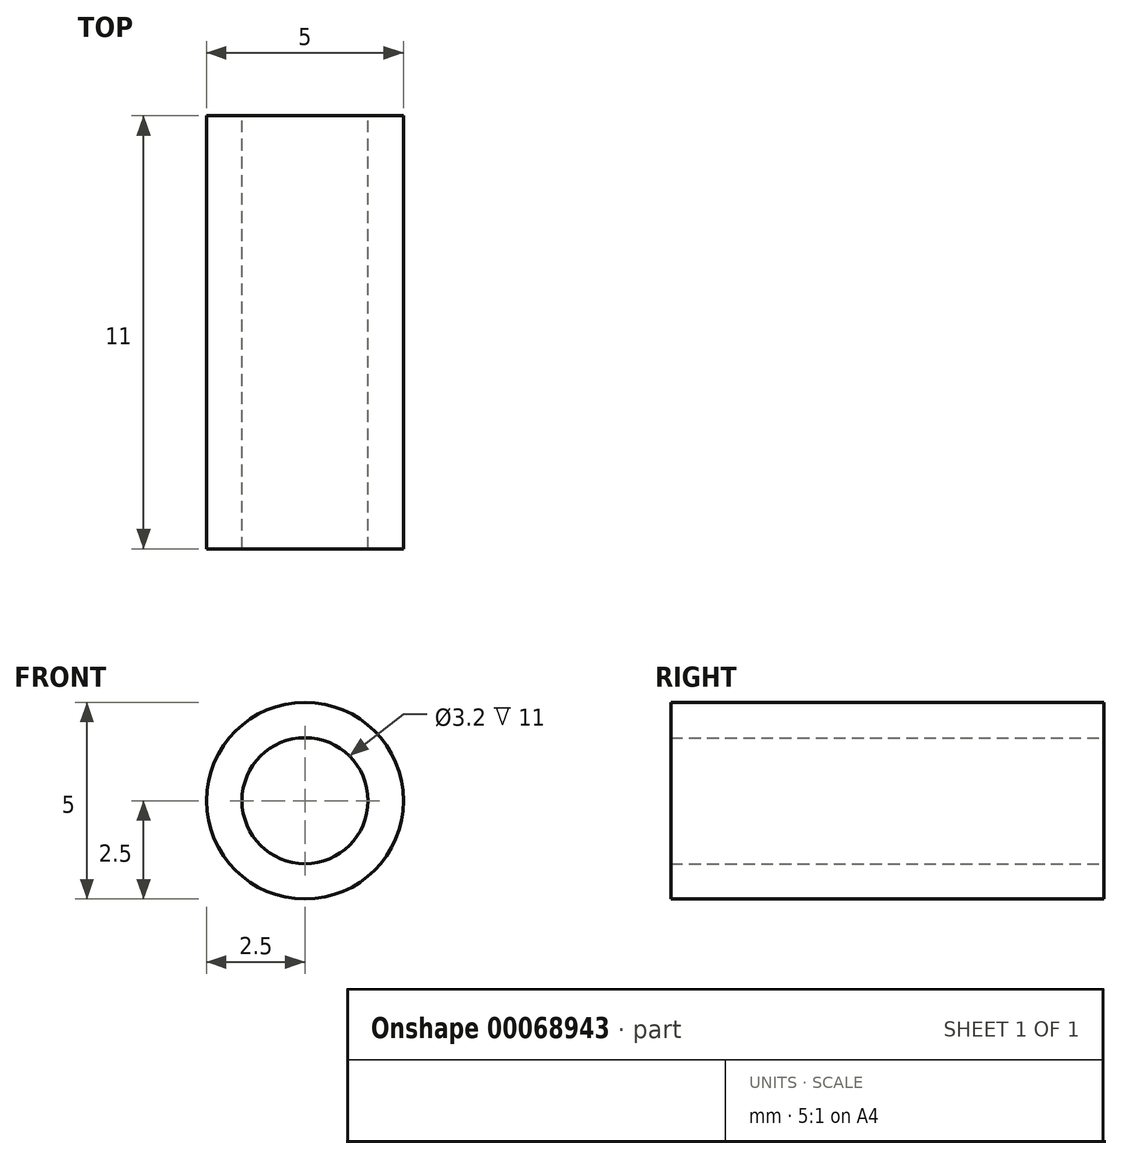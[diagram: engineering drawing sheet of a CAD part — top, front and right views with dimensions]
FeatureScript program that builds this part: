
annotation { "Feature Type Name" : "Feature", "Feature Type Description" : "" }
export const myFeature = defineFeature(function(context is Context, id is Id, definition is map)
    precondition{}
    {
        {
            var Q0;
            Q0=qCreatedBy(makeId("Front.planeOp"),FACE);
            var sketch = newSketch(context, id + "F0", { "sketchPlane" : qUnion([Q0])});
            skCircle(sketch, "E0", {"center": v(0, 0) * mm, "radius": 2.5 * mm});
            skCircle(sketch, "E1", {"center": v(0, 0) * mm, "radius": 1.6 * mm});
            skSolve(sketch);
        }
        {
            var Q0;
            Q0 = qSketchRegion(id + "F0", true);
            extrude(context, id + "F1", {"entities" : qUnion([Q0]), "depth" : 11 * mm});
        }
    });
